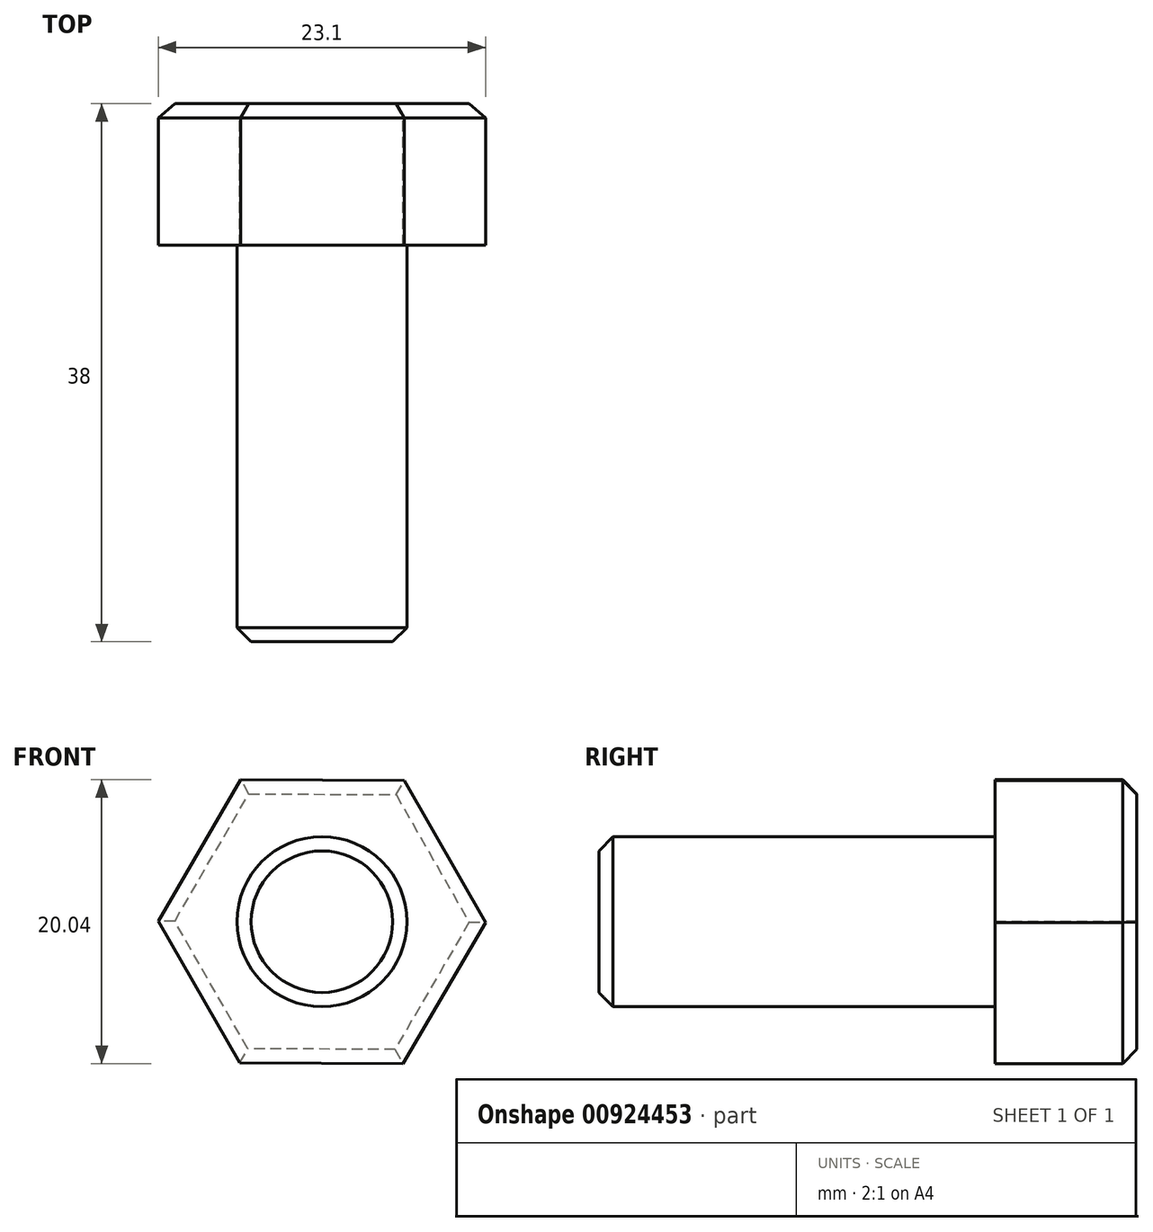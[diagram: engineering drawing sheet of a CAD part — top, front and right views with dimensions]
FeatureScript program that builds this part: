
annotation { "Feature Type Name" : "Feature", "Feature Type Description" : "" }
export const myFeature = defineFeature(function(context is Context, id is Id, definition is map)
    precondition{}
    {
        {
            var Q0;
            Q0=qCreatedBy(makeId("Front.planeOp"),FACE);
            var sketch = newSketch(context, id + "F0", { "sketchPlane" : qUnion([Q0])});
            skCircle(sketch, "E0.cCircle", {"center": v(0, 0) * mm, "radius": 10 * mm, "construction": true});
            skLineSegment(sketch, "E0.0", {"start": v(11.55, -0.05) * mm, "end": v(5.73, -10.02) * mm});
            skLineSegment(sketch, "E0.1", {"start": v(5.73, -10.02) * mm, "end": v(-5.82, -9.98) * mm});
            skLineSegment(sketch, "E0.2", {"start": v(-5.82, -9.98) * mm, "end": v(-11.55, 0.05) * mm});
            skLineSegment(sketch, "E0.3", {"start": v(-11.55, 0.05) * mm, "end": v(-5.73, 10.02) * mm});
            skLineSegment(sketch, "E0.4", {"start": v(-5.73, 10.02) * mm, "end": v(5.82, 9.98) * mm});
            skLineSegment(sketch, "E0.5", {"start": v(5.82, 9.98) * mm, "end": v(11.55, -0.05) * mm});
            skPoint(sketch, "E0.0.midPoint", {"position": v(8.64, -5.04) * mm});
            skSolve(sketch);
        }
        {
            var Q0;
            Q0=makeQuery(id+"F0.imprint","IMPRINT",FACE,{"disambiguationData":[TD([[makeQuery(id+"F0.imprint","IMPRINT",EDGE,{"derivedFrom":sQuery(id+"F0.wireOp",EDGE,"E0.0")}),-1.0]])]});
            extrude(context, id + "F1", {"entities" : qUnion([Q0]), "depth" : 10 * mm, "offsetDistance" : 25 * mm});
        }
        {
            var Q0;
            Q0=makeQuery(id+"F1.opExtrude","CAP_FACE",FACE,{"disambiguationData":[OSD([sQuery(id+"F0.wireOp",EDGE,"E0.0"),sQuery(id+"F0.wireOp",EDGE,"E0.1"),sQuery(id+"F0.wireOp",EDGE,"E0.2"),sQuery(id+"F0.wireOp",EDGE,"E0.3"),sQuery(id+"F0.wireOp",EDGE,"E0.4"),sQuery(id+"F0.wireOp",EDGE,"E0.5")])],"isStart":false});
            var sketch = newSketch(context, id + "F2", { "sketchPlane" : qUnion([Q0])});
            skCircle(sketch, "E1", {"center": v(0, 0) * mm, "radius": 6 * mm});
            skSolve(sketch);
        }
        {
            var Q0;
            Q0=makeQuery(id+"F2.imprint","IMPRINT",FACE,{"disambiguationData":[TD([[makeQuery(id+"F2.imprint","IMPRINT",EDGE,{"derivedFrom":sQuery(id+"F2.wireOp",EDGE,"E1")}),1.0]])]});
            extrude(context, id + "F3", {"entities" : qUnion([Q0]), "operationType" : NewBodyOperationType.ADD, "depth" : 28 * mm, "offsetDistance" : 25 * mm});
        }
        {
            var Q0;
            Q0=makeQuery(id+"F1.opExtrude","CAP_EDGE",EDGE,{"disambiguationData":[OSD([sQuery(id+"F0.wireOp",EDGE,"E0.3")])],"isStart":true});
            var Q1;
            Q1=makeQuery(id+"F1.opExtrude","CAP_EDGE",EDGE,{"disambiguationData":[OSD([sQuery(id+"F0.wireOp",EDGE,"E0.4")])],"isStart":true});
            var Q2;
            Q2=makeQuery(id+"F1.opExtrude","CAP_EDGE",EDGE,{"disambiguationData":[OSD([sQuery(id+"F0.wireOp",EDGE,"E0.5")])],"isStart":true});
            var Q3;
            Q3=makeQuery(id+"F1.opExtrude","CAP_EDGE",EDGE,{"disambiguationData":[OSD([sQuery(id+"F0.wireOp",EDGE,"E0.0")])],"isStart":true});
            var Q4;
            Q4=makeQuery(id+"F1.opExtrude","CAP_EDGE",EDGE,{"disambiguationData":[OSD([sQuery(id+"F0.wireOp",EDGE,"E0.1")])],"isStart":true});
            var Q5;
            Q5=makeQuery(id+"F1.opExtrude","CAP_EDGE",EDGE,{"disambiguationData":[OSD([sQuery(id+"F0.wireOp",EDGE,"E0.2")])],"isStart":true});
            var Q6;
            Q6=makeQuery(id+"F3.opExtrude","CAP_EDGE",EDGE,{"disambiguationData":[OSD([sQuery(id+"F2.wireOp",EDGE,"E1")])],"isStart":false});
            chamfer(context, id + "F4", {"entities" : qUnion([Q0, Q1, Q2, Q3, Q4, Q5, Q6]), "width" : 1 * mm, "tangentPropagation" : true});
        }
    });
